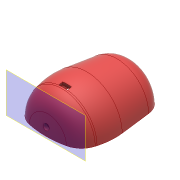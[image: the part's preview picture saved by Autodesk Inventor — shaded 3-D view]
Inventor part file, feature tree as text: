
AUTODESK INVENTOR PART (.ipt)
format: ipt  version: 2017 (Build 210142000, 142)  size: 257,024 bytes
history: native  units: mm
features: sketch x8, extrude x6, fillet x4, projected_geometry x2, revolve x1, chamfer x1, shell x1, hole x1, plane x1
ambient origin geometry x8: Origin, YZ Plane, XZ Plane, XY Plane, X Axis, Y Axis, Z Axis, Center Point
bodies: Solid1 (feature_tree)
feature tree (25):
  revolve  "Revolution1"  [1 undecoded]
  fillet  "Fillet1"  Radius=30.0mm
  chamfer  "Chamfer1"  Distance=10.0mm Angle=45.0deg
  fillet  "Fillet2"  Radius=20.0mm
  fillet  "Fillet3"  Radius=60.0mm
  extrude  "Extrusion1"  Depth=4.0mm
  shell  "Shell1"  Thickness=100.0mm
  extrude  "Extrusion3"  Depth=12.0mm
  extrude  "Extrusion4"  Depth=8.0mm
  hole  "Hole1"  [1 undecoded]
  plane  "Work Plane1"
  extrude  "Extrusion5"  [1 undecoded]
  fillet  "Fillet4"  Radius=6.0mm
  extrude  "Extrusion6"  Depth=4.0mm TaperAngle=0.0deg
  extrude  "Extrusion7"  Depth=9.0mm
  sketch  "Sketch1"  dims[d0=40.0mm d1=80.0mm d2=30.0mm]
  sketch  "Sketch2"  dims[d3=90.0deg]
  sketch  "Sketch4"  dims[d4=20.0mm d5=10.0mm d6=20.0mm d7=45.0deg d8=20.0mm d9=60.0mm]
  sketch  "Sketch5"  dims[d10=10.0mm d11=0.0mm d12=4.0mm d18=100.0mm d20=80.0mm]
  sketch  "Sketch6"  dims[d32=6.0mm d33=12.0mm]
  projected_geometry  "Projected Loop1"
  sketch  "Sketch7"  dims[d34=14.0mm d35=0.0mm d36=8.0mm]
  sketch  "Sketch8"  dims[d37=24.0mm d38=4.0mm d39=0.0mm]
  sketch  "Sketch9"  dims[d40=8.0mm d41=3.5mm d42=6.0mm d43=4.0mm d44=2.0mm d45=90.0deg d46=8.0mm d47=20.594885mm d48=-9.5mm d49=6.0mm d50=4.0mm d51=0.0mm d52=2.0mm d53=20.0mm d54=6.0mm d55=10.0mm d56=32.0mm d57=0.0mm d58=4.0mm d59=1.0mm d60=10.0mm d61=9.0mm d62=32.0mm d63=0.0mm]
  projected_geometry  "Projected Loop2"
note: 3 required parameter values undecoded (feature->parameter linkage not recoverable at this tier; creation-order binding heuristic only, values carry confidence <= 0.55)